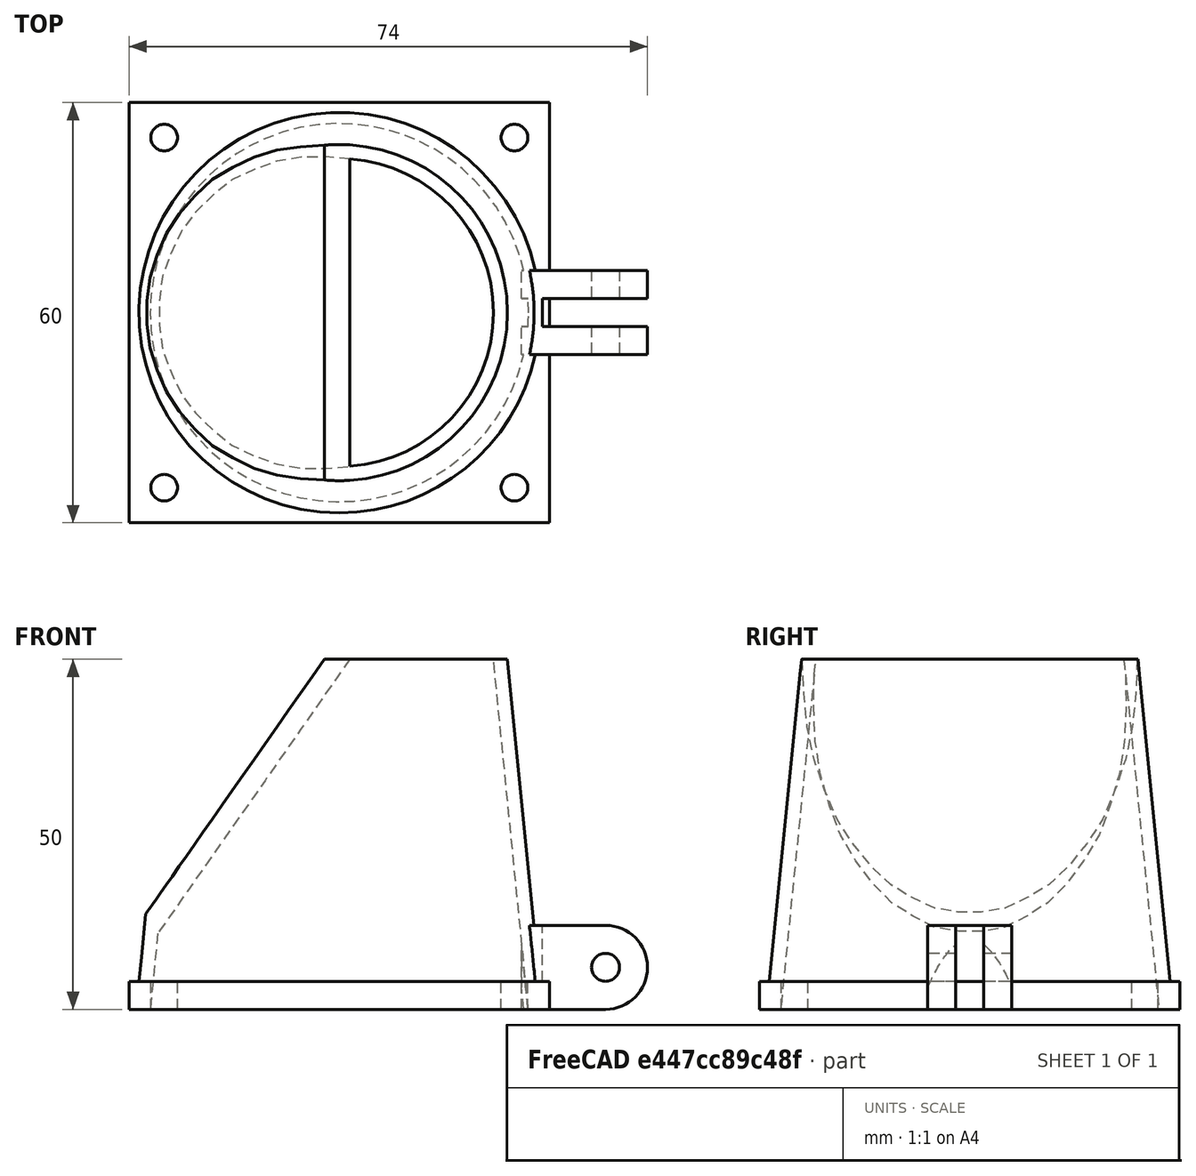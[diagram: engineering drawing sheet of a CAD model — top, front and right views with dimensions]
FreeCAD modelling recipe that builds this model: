
FCSTD DOCUMENT
Label: Fan_mount2
objects: Part::Cut×8, Part::Cylinder×6, Part::Fuse×6, Part::Box×5, Part::Cone×3, Mesh::Feature×1, Part::Common×1
note: 29 computed .brp shape members not serialized (recipe doc carries the construction recipe); baked Part::Feature solids carry a one-line shape summary decoded from their .brp

FEATURE [Mesh::Feature] fan_mount_fan
  Placement = pos=(-47,21,0) rot=(0,0,1;0rad)
FEATURE [Part::Box] Box
  Height = 4
  Length = 60
  Width = 60
FEATURE [Part::Cylinder] Cylinder
  Angle = 360
  Height = 10
  Placement = pos=(5,5,-4) rot=(0,0,1;0rad)
  Radius = 1.9
FEATURE [Part::Cylinder] Cylinder001
  Angle = 360
  Height = 10
  Placement = pos=(55,5,-4) rot=(0,0,1;0rad)
  Radius = 1.9
FEATURE [Part::Cylinder] Cylinder002
  Angle = 360
  Height = 10
  Placement = pos=(5,55,-4) rot=(0,0,1;0rad)
  Radius = 1.9
FEATURE [Part::Cylinder] Cylinder002001
  Angle = 360
  Height = 10
  Placement = pos=(55,55,-4) rot=(0,0,1;0rad)
  Radius = 1.9
FEATURE [Part::Cut] Cut
  Base = -> Box
  Tool = -> Cylinder
FEATURE [Part::Cut] Cut001
  Base = -> Cut
  Tool = -> Cylinder001
FEATURE [Part::Cut] Cut002
  Base = -> Cut001
  Tool = -> Cylinder002
FEATURE [Part::Cut] Cut003  label="Base1"
  Base = -> Cut002
  Tool = -> Cylinder002001
FEATURE [Part::Cone] Cone  label="Corps du duct"
  Angle = 360
  Height = 50
  Placement = pos=(30,30,0) rot=(0,0,1;0rad)
  Radius1 = 29
  Radius2 = 24
FEATURE [Part::Cone] Cone001  label="Trou principal"
  Angle = 360
  Height = 50
  Placement = pos=(30,30,0) rot=(0,0,1;0rad)
  Radius1 = 27
  Radius2 = 22
FEATURE [Part::Box] Box001
  Height = 3
  Length = 60
  Placement = pos=(0,0,5) rot=(0,-1,0;0.959932rad)
  Width = 60
FEATURE [Part::Cone] Cone002
  Angle = 360
  Height = 50
  Placement = pos=(30,30,0) rot=(0,0,1;0rad)
  Radius1 = 29
  Radius2 = 24
FEATURE [Part::Common] Common  label="Meplat"
  Base = -> Box001
  Tool = -> Cone002
FEATURE [Part::Box] Box001001  label="A retirer pour meplat"
  Height = 24
  Length = 60
  Placement = pos=(0,0,5) rot=(0,-1,0;0.959932rad)
  Width = 60
FEATURE [Part::Fuse] Fusion  label="Base2"
  Base = -> Cut003
  Tool = -> Cone
FEATURE [Part::Cut] Cut004  label="Base3"
  Base = -> Fusion
  Tool = -> Cone001
FEATURE [Part::Cut] Cut005  label="Base4"
  Base = -> Cut004
  Tool = -> Box001001
FEATURE [Part::Fuse] Fusion001  label="Base5"
  Base = -> Cut005
  Tool = -> Common
FEATURE [Part::Cylinder] Cylinder002002
  Angle = 360
  Height = 4
  Placement = pos=(68,28,6) rot=(1,0,0;1.5708rad)
  Radius = 6
FEATURE [Part::Cylinder] Cylinder002002001
  Angle = 360
  Height = 4
  Placement = pos=(68,28,6) rot=(1,0,0;1.5708rad)
  Radius = 2
FEATURE [Part::Box] Box001003  label="Plat languettes"
  Height = 12
  Length = 2
  Placement = pos=(57,24,0) rot=(0,0,1;0rad)
  Width = 12
FEATURE [Part::Box] Box001004
  Height = 12
  Length = 12
  Placement = pos=(56,24,0) rot=(0,0,1;0rad)
  Width = 4
FEATURE [Part::Fuse] Fusion002
  Base = -> Box001004
  Tool = -> Cylinder002002
FEATURE [Part::Cut] Cut006  label="Languette1"
  Base = -> Fusion002
  Tool = -> Cylinder002002001
FEATURE [Part::Cut] Cut006001  label="Languette002"
  Base = -> Fusion002
  Placement = pos=(0,8,0) rot=(0,0,1;0rad)
  Tool = -> Cylinder002002001
FEATURE [Part::Fuse] Fusion003
  Base = -> Box001003
  Tool = -> Cut006
FEATURE [Part::Fuse] Fusion004  label="Languette tot"
  Base = -> Fusion003
  Tool = -> Cut006001
FEATURE [Part::Fuse] Fusion005  label="Fan duct 2"
  Base = -> Fusion001
  Tool = -> Fusion004
